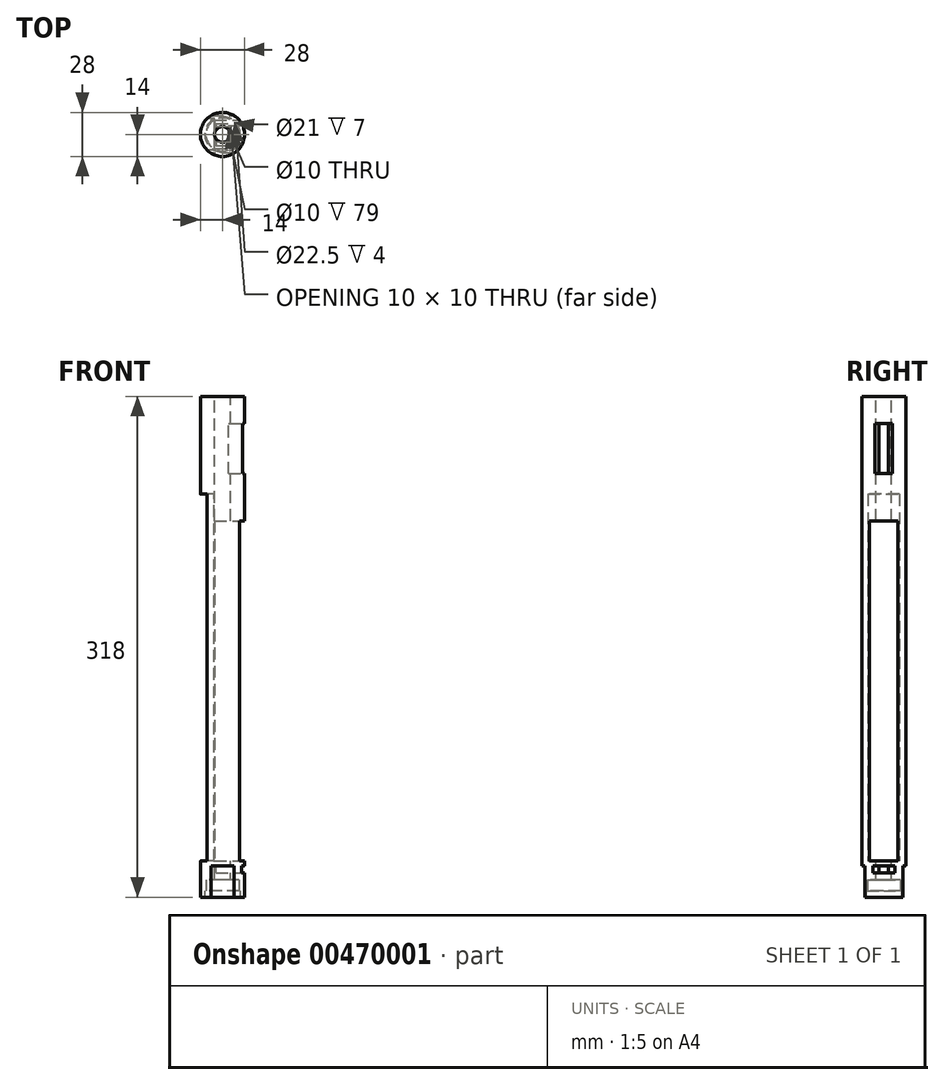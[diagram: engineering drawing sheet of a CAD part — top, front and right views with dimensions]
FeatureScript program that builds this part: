
annotation { "Feature Type Name" : "Feature", "Feature Type Description" : "" }
export const myFeature = defineFeature(function(context is Context, id is Id, definition is map)
    precondition{}
    {
        {
            var Q0;
            Q0=qCreatedBy(makeId("Top.planeOp"),FACE);
            var sketch = newSketch(context, id + "F0", { "sketchPlane" : qUnion([Q0])});
            skCircle(sketch, "E0", {"center": v(0, 0) * mm, "radius": 14 * mm});
            skSolve(sketch);
        }
        {
            var Q0;
            Q0 = qSketchRegion(id + "F0", true);
            extrude(context, id + "F1", {"entities" : qUnion([Q0]), "endBound" : BoundingType.SYMMETRIC, "depth" : 318 * mm});
        }
        {
            var Q0;
            Q0=qCreatedBy(makeId("Right.planeOp"),FACE);
            cPlane(context, id + "F2", {"entities" : qUnion([Q0]), "cplaneType" : CPlaneType.OFFSET, "offset" : (28 / 2) * mm, "width" : 150 * mm, "height" : 150 * mm});
        }
        {
            var Q0;
            Q0=qCreatedBy(id+"F2.planeOp",FACE);
            var sketch = newSketch(context, id + "F3", { "sketchPlane" : qUnion([Q0])});
            skLineSegment(sketch, "E1.bottom", {"start": v(9, 80) * mm, "end": v(-9, 80) * mm});
            skPoint(sketch, "E1.middle", {"position": v(0, 47.5) * mm});
            skPoint(sketch, "E2.middle", {"position": v(0, -35) * mm});
            skLineSegment(sketch, "E3.top", {"start": v(9, -136) * mm, "end": v(-9, -136) * mm});
            skPoint(sketch, "E3.middle", {"position": v(0, -102) * mm});
            skLineSegment(sketch, "E4.bottom", {"start": v(7, -139) * mm, "end": v(-7, -139) * mm});
            skLineSegment(sketch, "E4.top", {"start": v(7, -143.5) * mm, "end": v(-7, -143.5) * mm});
            skLineSegment(sketch, "E4.left", {"start": v(7, -139) * mm, "end": v(7, -143.5) * mm});
            skLineSegment(sketch, "E4.right", {"start": v(-7, -139) * mm, "end": v(-7, -143.5) * mm});
            skPoint(sketch, "E4.middle", {"position": v(0, -141.25) * mm});
            skLineSegment(sketch, "E5.bottom", {"start": v(5.5, 110) * mm, "end": v(-5.5, 110) * mm});
            skLineSegment(sketch, "E5.top", {"start": v(5.5, 142) * mm, "end": v(-5.5, 142) * mm});
            skLineSegment(sketch, "E5.left", {"start": v(5.5, 110) * mm, "end": v(5.5, 142) * mm});
            skLineSegment(sketch, "E5.right", {"start": v(-5.5, 110) * mm, "end": v(-5.5, 142) * mm});
            skPoint(sketch, "E5.middle", {"position": v(0, 126) * mm});
            skLineSegment(sketch, "E6", {"start": v(9, 80) * mm, "end": v(9, -136) * mm});
            skLineSegment(sketch, "E7", {"start": v(-9, -136) * mm, "end": v(-9, 80) * mm});
            skSolve(sketch);
        }
        {
            var Q0;
            Q0=makeQuery(id+"F3.imprint","IMPRINT",FACE,{"disambiguationData":[TD([[makeQuery(id+"F3.imprint","IMPRINT",EDGE,{"derivedFrom":sQuery(id+"F3.wireOp",EDGE,"E1.bottom")}),1.0]])]});
            extrude(context, id + "F4", {"entities" : qUnion([Q0]), "operationType" : NewBodyOperationType.REMOVE, "oppositeDirection" : true, "offsetDistance" : 25 * mm, "depth" : 19 * mm});
        }
        {
            var Q0;
            Q0=makeQuery(id+"F3.imprint","IMPRINT",FACE,{"disambiguationData":[TD([[makeQuery(id+"F3.imprint","IMPRINT",EDGE,{"derivedFrom":sQuery(id+"F3.wireOp",EDGE,"E4.bottom")}),1.0]])]});
            extrude(context, id + "F5", {"entities" : qUnion([Q0]), "operationType" : NewBodyOperationType.REMOVE, "oppositeDirection" : true, "offsetDistance" : 25 * mm, "depth" : 18 * mm});
        }
        {
            var Q0;
            Q0=qCreatedBy(makeId("Right.planeOp"),FACE);
            cPlane(context, id + "F6", {"entities" : qUnion([Q0]), "cplaneType" : CPlaneType.OFFSET, "offset" : 14 * mm, "oppositeDirection" : true, "width" : 150 * mm, "height" : 150 * mm});
        }
        {
            var Q0;
            Q0=qCreatedBy(id+"F6.planeOp",FACE);
            var sketch = newSketch(context, id + "F7", { "sketchPlane" : qUnion([Q0])});
            skLineSegment(sketch, "E8.bottom", {"start": v(-10, -136) * mm, "end": v(10, -136) * mm});
            skLineSegment(sketch, "E8.top", {"start": v(-10, -98) * mm, "end": v(10, -98) * mm});
            skLineSegment(sketch, "E8.left", {"start": v(-10, -136) * mm, "end": v(-10, -98) * mm});
            skLineSegment(sketch, "E8.right", {"start": v(10, -136) * mm, "end": v(10, -98) * mm});
            skPoint(sketch, "E8.middle", {"position": v(0, -117) * mm});
            skLineSegment(sketch, "E9.bottom", {"start": v(-10, -75) * mm, "end": v(10, -75) * mm});
            skLineSegment(sketch, "E9.top", {"start": v(-10, -46) * mm, "end": v(10, -46) * mm});
            skLineSegment(sketch, "E9.left", {"start": v(-10, -75) * mm, "end": v(-10, -46) * mm});
            skLineSegment(sketch, "E9.right", {"start": v(10, -75) * mm, "end": v(10, -46) * mm});
            skPoint(sketch, "E9.middle", {"position": v(0, -60.5) * mm});
            skLineSegment(sketch, "E10.bottom", {"start": v(-10, -23) * mm, "end": v(10, -23) * mm});
            skLineSegment(sketch, "E10.top", {"start": v(-10, 2) * mm, "end": v(10, 2) * mm});
            skLineSegment(sketch, "E10.left", {"start": v(-10, -23) * mm, "end": v(-10, 2) * mm});
            skLineSegment(sketch, "E10.right", {"start": v(10, -23) * mm, "end": v(10, 2) * mm});
            skPoint(sketch, "E10.middle", {"position": v(0, -10.5) * mm});
            skLineSegment(sketch, "E11.bottom", {"start": v(-10, 25) * mm, "end": v(10, 25) * mm});
            skLineSegment(sketch, "E11.top", {"start": v(-10, 47) * mm, "end": v(10, 47) * mm});
            skLineSegment(sketch, "E11.left", {"start": v(-10, 25) * mm, "end": v(-10, 47) * mm});
            skLineSegment(sketch, "E11.right", {"start": v(10, 25) * mm, "end": v(10, 47) * mm});
            skPoint(sketch, "E11.middle", {"position": v(0, 36) * mm});
            skLineSegment(sketch, "E12.bottom", {"start": v(2.5, 47) * mm, "end": v(-2.5, 47) * mm});
            skLineSegment(sketch, "E12.top", {"start": v(2.5, -136) * mm, "end": v(-2.5, -136) * mm});
            skLineSegment(sketch, "E13", {"start": v(10, 25) * mm, "end": v(10, 2) * mm});
            skLineSegment(sketch, "E14", {"start": v(-10, 25) * mm, "end": v(-10, 2) * mm});
            skLineSegment(sketch, "E15", {"start": v(10, -23) * mm, "end": v(10, -46) * mm});
            skLineSegment(sketch, "E16", {"start": v(-10, -23) * mm, "end": v(-10, -46) * mm});
            skLineSegment(sketch, "E17", {"start": v(10, -75) * mm, "end": v(10, -98) * mm});
            skLineSegment(sketch, "E18", {"start": v(-10, -75) * mm, "end": v(-10, -98) * mm});
            skLineSegment(sketch, "E19.bottom", {"start": v(10, 47) * mm, "end": v(-10, 47) * mm});
            skLineSegment(sketch, "E19.top", {"start": v(10, 97) * mm, "end": v(-10, 97) * mm});
            skLineSegment(sketch, "E19.left", {"start": v(10, 47) * mm, "end": v(10, 97) * mm});
            skLineSegment(sketch, "E19.right", {"start": v(-10, 47) * mm, "end": v(-10, 97) * mm});
            skSolve(sketch);
        }
        {
            var Q0;
            Q0=makeQuery(id+"F7.imprint","IMPRINT",FACE,{"disambiguationData":[TD([[makeQuery(id+"F7.imprint","IMPRINT",EDGE,{"derivedFrom":sQuery(id+"F7.wireOp",EDGE,"E8.bottom")}),1.0]])]});
            var Q1;
            Q1=makeQuery(id+"F7.imprint","IMPRINT",FACE,{"disambiguationData":[TD([[makeQuery(id+"F7.imprint","IMPRINT",EDGE,{"derivedFrom":sQuery(id+"F7.wireOp",EDGE,"E9.bottom")}),1.0]])]});
            var Q2;
            Q2=makeQuery(id+"F7.imprint","IMPRINT",FACE,{"disambiguationData":[TD([[makeQuery(id+"F7.imprint","IMPRINT",EDGE,{"derivedFrom":sQuery(id+"F7.wireOp",EDGE,"E10.bottom")}),1.0]])]});
            var Q3;
            Q3=makeQuery(id+"F7.imprint","IMPRINT",FACE,{"disambiguationData":[TD([[makeQuery(id+"F7.imprint","IMPRINT",EDGE,{"derivedFrom":sQuery(id+"F7.wireOp",EDGE,"E11.bottom")}),1.0]])]});
            var Q4;
            {var subQ5=sQuery(id+"F7.wireOp",EDGE,"E12.top");Q4=makeQuery(id+"F7.imprint","IMPRINT",FACE,{"disambiguationData":[TD([[makeQuery(id+"F7.imprint","IMPRINT",EDGE,{"derivedFrom":subQ5}),-1.0]])]});}
            var Q5;
            Q5=makeQuery(id+"F7.imprint","IMPRINT",FACE,{"disambiguationData":[TD([[makeQuery(id+"F7.imprint","IMPRINT",EDGE,{"derivedFrom":sQuery(id+"F7.wireOp",EDGE,"E8.top")}),1.0]])]});
            var Q6;
            Q6=makeQuery(id+"F7.imprint","IMPRINT",FACE,{"disambiguationData":[TD([[makeQuery(id+"F7.imprint","IMPRINT",EDGE,{"derivedFrom":sQuery(id+"F7.wireOp",EDGE,"E9.top")}),1.0]])]});
            var Q7;
            Q7=makeQuery(id+"F7.imprint","IMPRINT",FACE,{"disambiguationData":[TD([[makeQuery(id+"F7.imprint","IMPRINT",EDGE,{"derivedFrom":sQuery(id+"F7.wireOp",EDGE,"E10.top")}),1.0]])]});
            var Q8;
            Q8=makeQuery(id+"F7.imprint","IMPRINT",FACE,{"disambiguationData":[TD([[makeQuery(id+"F7.imprint","IMPRINT",EDGE,{"derivedFrom":sQuery(id+"F7.wireOp",EDGE,"E19.top")}),1.0]])]});
            extrude(context, id + "F8", {"entities" : qUnion([Q0, Q1, Q2, Q3, Q4, Q5, Q6, Q7, Q8]), "operationType" : NewBodyOperationType.REMOVE, "depth" : 8.6 * mm});
        }
        {
            var Q0;
            Q0=makeQuery(id+"F3.imprint","IMPRINT",FACE,{"disambiguationData":[TD([[makeQuery(id+"F3.imprint","IMPRINT",EDGE,{"derivedFrom":sQuery(id+"F3.wireOp",EDGE,"E5.bottom")}),-1.0]])]});
            extrude(context, id + "F9", {"entities" : qUnion([Q0]), "operationType" : NewBodyOperationType.REMOVE, "oppositeDirection" : true, "depth" : 10 * mm, "offsetDistance" : 25 * mm});
        }
        {
            var Q0;
            Q0=qCreatedBy(makeId("Top.planeOp"),FACE);
            cPlane(context, id + "F10", {"entities" : qUnion([Q0]), "cplaneType" : CPlaneType.OFFSET, "offset" : (318 / 2) * mm, "width" : 150 * mm, "height" : 150 * mm});
        }
        {
            var Q0;
            Q0=qCreatedBy(id+"F10.planeOp",FACE);
            var sketch = newSketch(context, id + "F11", { "sketchPlane" : qUnion([Q0])});
            skCircle(sketch, "E20", {"center": v(0, 0) * mm, "radius": 5 * mm});
            skSolve(sketch);
        }
        {
            var Q0;
            Q0=qCreatedBy(makeId("Top.planeOp"),FACE);
            cPlane(context, id + "F12", {"entities" : qUnion([Q0]), "cplaneType" : CPlaneType.OFFSET, "offset" : (318 / 2) * mm, "oppositeDirection" : true, "width" : 150 * mm, "height" : 150 * mm});
        }
        {
            var Q0;
            Q0=qCreatedBy(id+"F12.planeOp",FACE);
            var sketch = newSketch(context, id + "F13", { "sketchPlane" : qUnion([Q0])});
            skCircle(sketch, "E21", {"center": v(0, 0) * mm, "radius": 10.5 * mm});
            skCircle(sketch, "E22", {"center": v(0, 0) * mm, "radius": 11.25 * mm});
            skCircle(sketch, "E23", {"center": v(0, 0) * mm, "radius": 14 * mm});
            skLineSegment(sketch, "E24", {"start": v(0, -14) * mm, "end": v(0, -12) * mm});
            skLineSegment(sketch, "E25", {"start": v(7.21, -12) * mm, "end": v(-7.21, -12) * mm});
            skLineSegment(sketch, "E26.1.0", {"start": v(-7.21, 12) * mm, "end": v(7.21, 12) * mm});
            skSolve(sketch);
        }
        {
            var Q0;
            Q0=makeQuery(id+"F13.imprint","IMPRINT",FACE,{"disambiguationData":[TD([[makeQuery(id+"F13.imprint","IMPRINT",EDGE,{"derivedFrom":sQuery(id+"F13.wireOp",EDGE,"E21")}),1.0]])]});
            var Q1;
            Q1=makeQuery(id+"F13.imprint","IMPRINT",FACE,{"disambiguationData":[TD([[makeQuery(id+"F13.imprint","IMPRINT",EDGE,{"derivedFrom":sQuery(id+"F13.wireOp",EDGE,"E21")}),1.0]])]});
            extrude(context, id + "F14", {"entities" : qUnion([Q0, Q1]), "operationType" : NewBodyOperationType.REMOVE, "offsetDistance" : 25 * mm, "depth" : 11 * mm});
        }
        {
            var Q0;
            Q0=makeQuery(id+"F11.imprint","IMPRINT",FACE,{"disambiguationData":[TD([[makeQuery(id+"F11.imprint","IMPRINT",EDGE,{"derivedFrom":sQuery(id+"F11.wireOp",EDGE,"E20")}),1.0]])]});
            extrude(context, id + "F15", {"entities" : qUnion([Q0]), "operationType" : NewBodyOperationType.REMOVE, "oppositeDirection" : true, "depth" : 318 * mm});
        }
        {
            var Q0;
            Q0=makeQuery(id+"F13.imprint","IMPRINT",FACE,{"disambiguationData":[TD([[makeQuery(id+"F13.imprint","IMPRINT",EDGE,{"derivedFrom":sQuery(id+"F13.wireOp",EDGE,"E21")}),-1.0]])]});
            extrude(context, id + "F16", {"entities" : qUnion([Q0]), "operationType" : NewBodyOperationType.REMOVE, "depth" : 4 * mm, "offsetDistance" : 25 * mm});
        }
        {
            var Q0;
            {var subQ0=sQuery(id+"F13.wireOp",EDGE,"E24");Q0=makeQuery(id+"F13.imprint","IMPRINT",FACE,{"disambiguationData":[TD([[makeQuery(id+"F13.imprint","IMPRINT",EDGE,{"derivedFrom":subQ0}),1.0]])]});}
            var Q1;
            {var subQ0=sQuery(id+"F13.wireOp",EDGE,"E24");Q1=makeQuery(id+"F13.imprint","IMPRINT",FACE,{"disambiguationData":[TD([[makeQuery(id+"F13.imprint","IMPRINT",EDGE,{"derivedFrom":subQ0}),-1.0]])]});}
            var Q2;
            {var subQ0=sQuery(id+"F13.wireOp",EDGE,"E26.1.0");Q2=makeQuery(id+"F13.imprint","IMPRINT",FACE,{"disambiguationData":[TD([[makeQuery(id+"F13.imprint","IMPRINT",EDGE,{"derivedFrom":subQ0}),1.0]])]});}
            extrude(context, id + "F17", {"entities" : qUnion([Q0, Q1, Q2]), "operationType" : NewBodyOperationType.REMOVE, "depth" : 20 * mm, "offsetDistance" : 25 * mm});
        }
    });
